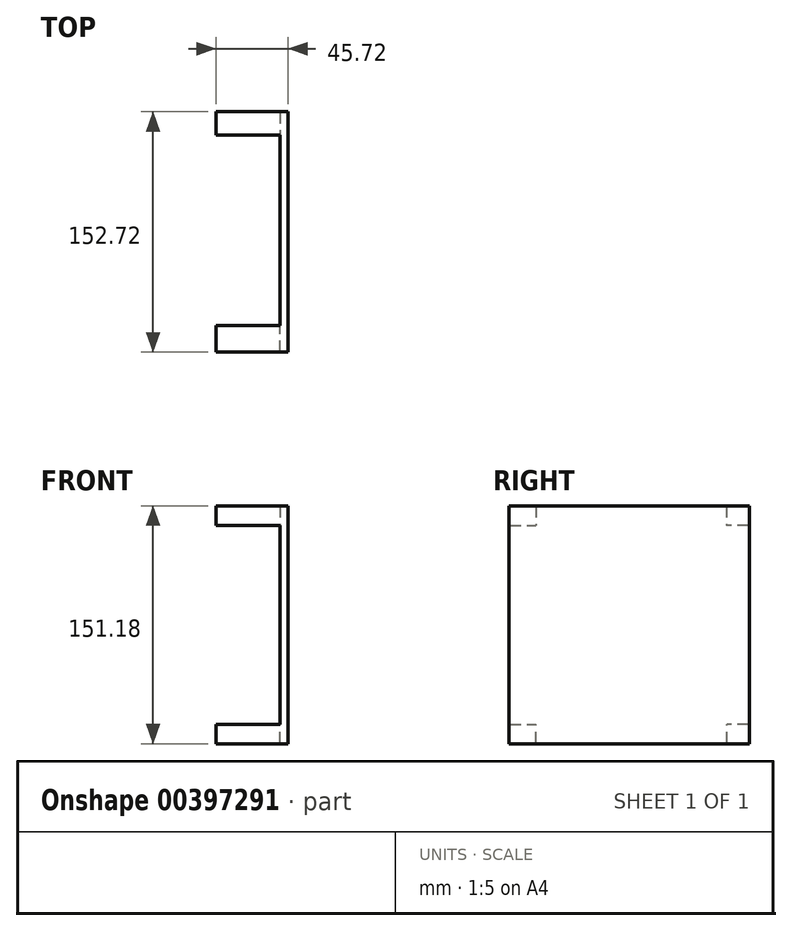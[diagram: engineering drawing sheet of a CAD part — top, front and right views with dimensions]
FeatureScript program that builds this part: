
annotation { "Feature Type Name" : "Feature", "Feature Type Description" : "" }
export const myFeature = defineFeature(function(context is Context, id is Id, definition is map)
    precondition{}
    {
        {
            var Q0;
            Q0=qCreatedBy(makeId("Right.planeOp"),FACE);
            var sketch = newSketch(context, id + "F0", { "sketchPlane" : qUnion([Q0])});
            skLineSegment(sketch, "E0.bottom", {"start": v(-76.08, 75.45) * mm, "end": v(76.64, 75.45) * mm});
            skLineSegment(sketch, "E0.top", {"start": v(-76.08, -75.73) * mm, "end": v(76.64, -75.73) * mm});
            skLineSegment(sketch, "E0.left", {"start": v(-76.08, 75.45) * mm, "end": v(-76.08, -75.73) * mm});
            skLineSegment(sketch, "E0.right", {"start": v(76.64, 75.45) * mm, "end": v(76.64, -75.73) * mm});
            skSolve(sketch);
        }
        {
            var Q0;
            Q0=makeQuery(id+"F0.imprint","IMPRINT",FACE,{"disambiguationData":[TD([[makeQuery(id+"F0.imprint","IMPRINT",EDGE,{"derivedFrom":sQuery(id+"F0.wireOp",EDGE,"E0.bottom")}),-1.0]])]});
            extrude(context, id + "F1", {"entities" : qUnion([Q0]), "depth" : 5.08 * mm});
        }
        {
            var Q0;
            Q0=makeQuery(id+"F1.opExtrude","CAP_FACE",FACE,{"disambiguationData":[OSD([sQuery(id+"F0.wireOp",EDGE,"E0.bottom"),sQuery(id+"F0.wireOp",EDGE,"E0.top"),sQuery(id+"F0.wireOp",EDGE,"E0.left"),sQuery(id+"F0.wireOp",EDGE,"E0.right")])],"isStart":true});
            var sketch = newSketch(context, id + "F2", { "sketchPlane" : qUnion([Q0])});
            skLineSegment(sketch, "E1.bottom", {"start": v(76.08, 75.45) * mm, "end": v(59.03, 75.45) * mm});
            skLineSegment(sketch, "E1.top", {"start": v(76.08, 62.78) * mm, "end": v(59.03, 62.78) * mm});
            skLineSegment(sketch, "E1.left", {"start": v(76.08, 75.45) * mm, "end": v(76.08, 62.78) * mm});
            skLineSegment(sketch, "E1.right", {"start": v(59.03, 75.45) * mm, "end": v(59.03, 62.78) * mm});
            skLineSegment(sketch, "E2.bottom", {"start": v(76.08, -75.73) * mm, "end": v(59.03, -75.73) * mm});
            skLineSegment(sketch, "E2.top", {"start": v(76.08, -63.57) * mm, "end": v(59.03, -63.57) * mm});
            skLineSegment(sketch, "E2.left", {"start": v(76.08, -75.73) * mm, "end": v(76.08, -63.57) * mm});
            skLineSegment(sketch, "E2.right", {"start": v(59.03, -75.73) * mm, "end": v(59.03, -63.57) * mm});
            skLineSegment(sketch, "E3.bottom", {"start": v(-76.64, 75.45) * mm, "end": v(-62.01, 75.45) * mm});
            skLineSegment(sketch, "E3.top", {"start": v(-76.64, 62.78) * mm, "end": v(-62.01, 62.78) * mm});
            skLineSegment(sketch, "E3.left", {"start": v(-76.64, 75.45) * mm, "end": v(-76.64, 62.78) * mm});
            skLineSegment(sketch, "E3.right", {"start": v(-62.01, 75.45) * mm, "end": v(-62.01, 62.78) * mm});
            skLineSegment(sketch, "E4.bottom", {"start": v(-76.64, -75.73) * mm, "end": v(-62.24, -75.73) * mm});
            skLineSegment(sketch, "E4.top", {"start": v(-76.64, -63.57) * mm, "end": v(-62.24, -63.57) * mm});
            skLineSegment(sketch, "E4.left", {"start": v(-76.64, -75.73) * mm, "end": v(-76.64, -63.57) * mm});
            skLineSegment(sketch, "E4.right", {"start": v(-62.24, -75.73) * mm, "end": v(-62.24, -63.57) * mm});
            skSolve(sketch);
        }
        {
            var Q0;
            Q0 = qSketchRegion(id + "F2", true);
            extrude(context, id + "F3", {"entities" : qUnion([Q0]), "operationType" : NewBodyOperationType.ADD, "depth" : 40.64 * mm});
        }
    });
